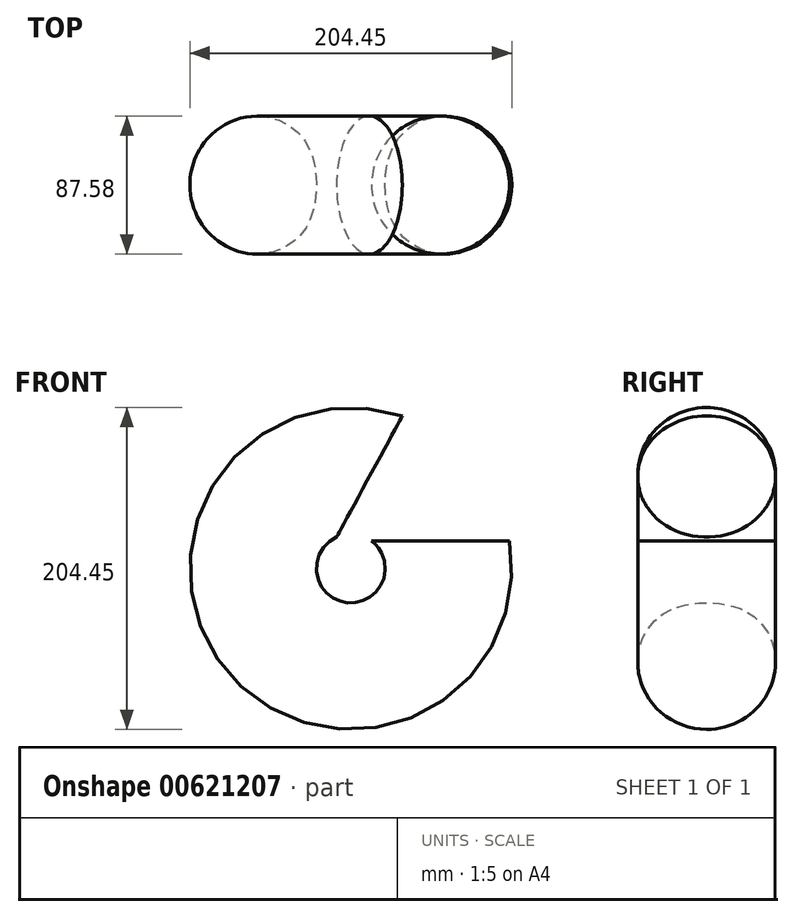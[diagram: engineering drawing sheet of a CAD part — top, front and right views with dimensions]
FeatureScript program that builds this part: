
annotation { "Feature Type Name" : "Feature", "Feature Type Description" : "" }
export const myFeature = defineFeature(function(context is Context, id is Id, definition is map)
    precondition{}
    {
        {
            var Q0;
            Q0=qCreatedBy(makeId("Top.planeOp"),FACE);
            var sketch = newSketch(context, id + "F0", { "sketchPlane" : qUnion([Q0])});
            skCircle(sketch, "E0", {"center": v(43.79, 0) * mm, "radius": 43.79 * mm});
            skSolve(sketch);
        }
        {
            var Q0;
            Q0=qCreatedBy(makeId("Front.planeOp"),FACE);
            var sketch = newSketch(context, id + "F1", { "sketchPlane" : qUnion([Q0])});
            skArc(sketch, "E1", {"start": v(0, 43.37) * mm, "mid": v(-55.56, -63.04) * mm, "end": v(46.6, 0) * mm});
            skSolve(sketch);
        }
        {
            var Q0;
            Q0=makeQuery(id+"F0.imprint","IMPRINT",FACE,{"disambiguationData":[TD([[makeQuery(id+"F0.imprint","IMPRINT",EDGE,{"derivedFrom":sQuery(id+"F0.wireOp",EDGE,"E0")}),1.0]])]});
            var Q1;
            Q1=sQuery(id+"F1.wireOp",EDGE,"E1");
            sweep(context, id + "F2", {"profiles" : qUnion([Q0]), "path" : qUnion([Q1])});
        }
    });
